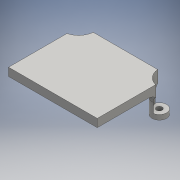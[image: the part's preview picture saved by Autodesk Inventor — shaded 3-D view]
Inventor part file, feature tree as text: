
AUTODESK INVENTOR PART (.ipt)
format: ipt  version: 2016 (Build 200138000, 138)  size: 185,856 bytes
history: native  units: mm
features: extrude x4, sketch x4, projected_geometry x3, mirror x2, fillet x1
ambient origin geometry x8: Origin, YZ Plane, XZ Plane, XY Plane, X Axis, Y Axis, Z Axis, Center Point
bodies: Solid1 (feature_tree)
feature tree (14):
  extrude  "Extrusion1"  Depth=45.0mm
  extrude  "Extrusion2"  Depth=20.0mm TaperAngle=0.0deg
  extrude  "Extrusion4"  Depth=6.0mm
  extrude  "Extrusion5"  Depth=6.0mm TaperAngle=0.0deg
  mirror  "Mirror2"
  fillet  "Fillet1"  Radius=3.5mm
  mirror  "Mirror3"
  sketch  "Sketch1"  dims[d0=55.0mm d1=45.0mm]
  sketch  "Sketch2"  dims[d2=5.0mm d3=0.0mm d6=20.0mm d7=0.0mm]
  projected_geometry  "Projected Loop1"
  sketch  "Sketch3"  dims[d11=6.0mm d19=9.0mm]
  projected_geometry  "Projected Loop2"
  sketch  "Sketch5"  dims[d20=9.0mm d25=17.0mm d26=0.0mm d27=3.5mm d28=17.0mm d29=0.0mm d30=49.0mm d31=3.5mm d32=6.0mm]
  projected_geometry  "Projected Loop4"
